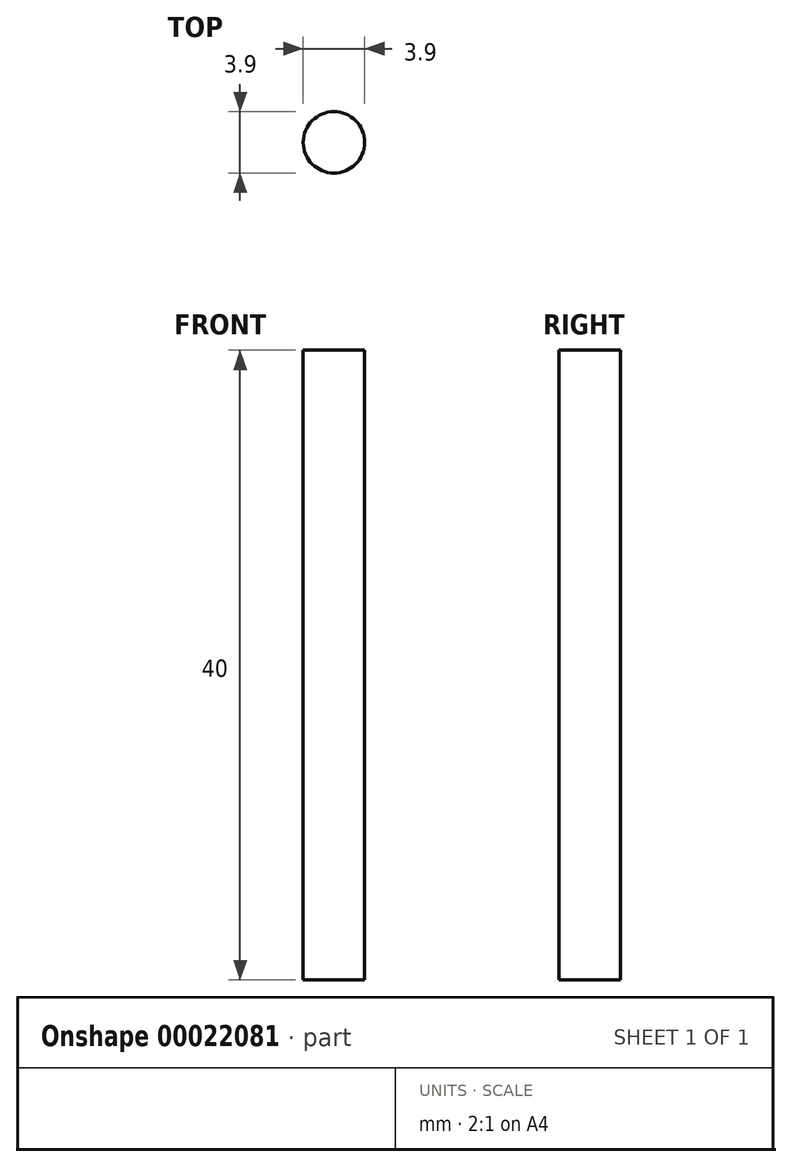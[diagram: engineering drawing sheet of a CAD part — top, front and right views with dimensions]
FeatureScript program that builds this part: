
annotation { "Feature Type Name" : "Feature", "Feature Type Description" : "" }
export const myFeature = defineFeature(function(context is Context, id is Id, definition is map)
    precondition{}
    {
        {
            var Q0;
            Q0=qCreatedBy(makeId("Front.planeOp"),FACE);
            var sketch = newSketch(context, id + "F0", { "sketchPlane" : qUnion([Q0])});
            skLineSegment(sketch, "E0.left", {"start": v(-11.24, 23.25) * mm, "end": v(-11.24, -16.75) * mm});
            skLineSegment(sketch, "E0.right", {"start": v(-9.3, 23.25) * mm, "end": v(-9.3, -16.75) * mm});
            skLineSegment(sketch, "E1", {"start": v(-11.24, 23.25) * mm, "end": v(-9.3, 23.25) * mm});
            skLineSegment(sketch, "E2", {"start": v(-11.24, -16.75) * mm, "end": v(-9.3, -16.75) * mm});
            skSolve(sketch);
        }
        {
            var Q0;
            Q0=makeQuery(id+"F0.imprint","IMPRINT",FACE,{"disambiguationData":[TD([[makeQuery(id+"F0.imprint","IMPRINT",EDGE,{"derivedFrom":sQuery(id+"F0.wireOp",EDGE,"E0.left")}),1.0]])]});
            var Q1;
            Q1=sQuery(id+"F0.wireOp",EDGE,"E0.left");
            revolve(context, id + "F1", {"entities" : qUnion([Q0]), "axis" : qUnion([Q1]), "revolveType" : RevolveType.FULL});
        }
    });
